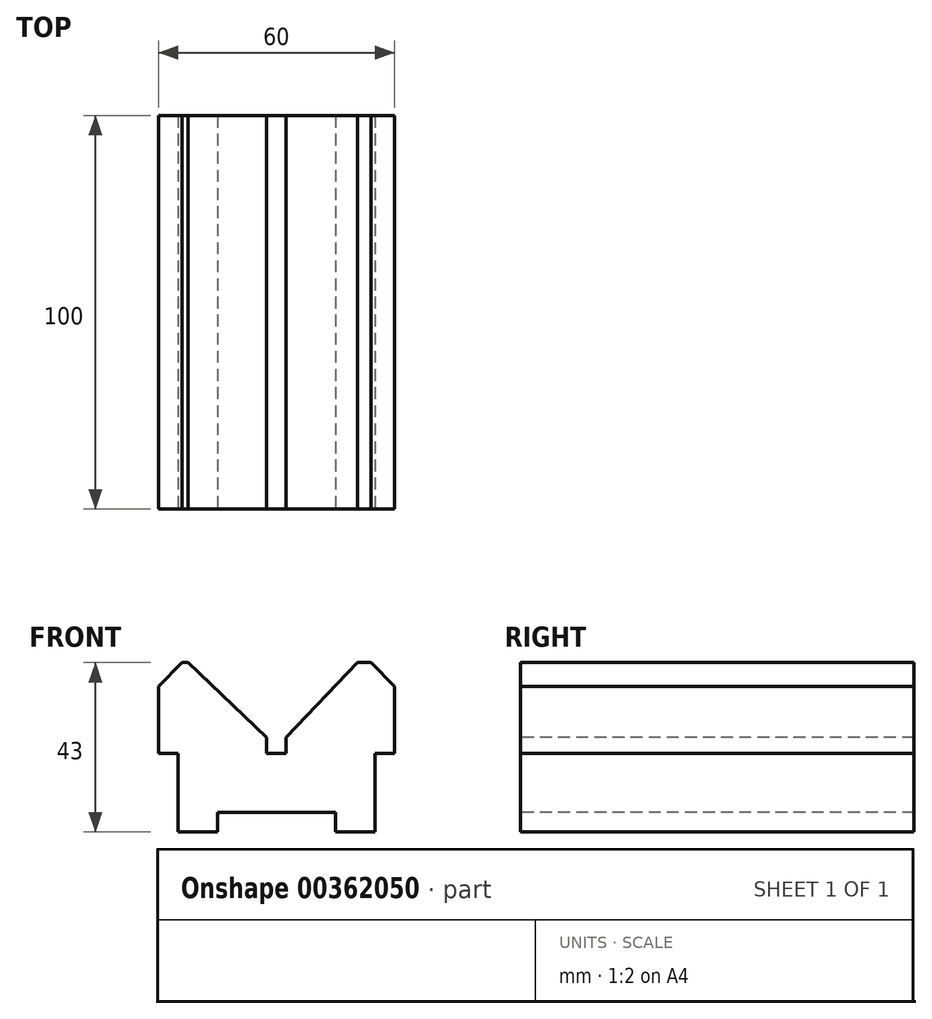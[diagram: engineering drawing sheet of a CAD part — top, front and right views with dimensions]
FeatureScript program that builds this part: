
annotation { "Feature Type Name" : "Feature", "Feature Type Description" : "" }
export const myFeature = defineFeature(function(context is Context, id is Id, definition is map)
    precondition{}
    {
        {
            var Q0;
            Q0=qCreatedBy(makeId("Front.planeOp"),FACE);
            var sketch = newSketch(context, id + "F0", { "sketchPlane" : qUnion([Q0])});
            skLineSegment(sketch, "E0", {"start": v(-24.1, 0) * mm, "end": v(-14.1, 0) * mm});
            skLineSegment(sketch, "E1", {"start": v(-14.1, 0) * mm, "end": v(-14.1, 5) * mm});
            skLineSegment(sketch, "E2", {"start": v(-14.1, 5) * mm, "end": v(15.9, 5) * mm});
            skLineSegment(sketch, "E3", {"start": v(15.9, 5) * mm, "end": v(15.9, 0) * mm});
            skLineSegment(sketch, "E4", {"start": v(15.9, 0) * mm, "end": v(25.9, 0) * mm});
            skLineSegment(sketch, "E5", {"start": v(25.9, 0) * mm, "end": v(25.9, 20) * mm});
            skLineSegment(sketch, "E6", {"start": v(25.9, 20) * mm, "end": v(30.9, 20) * mm});
            skLineSegment(sketch, "E7", {"start": v(30.9, 20) * mm, "end": v(30.9, 37) * mm});
            skLineSegment(sketch, "E8", {"start": v(21.52, 43) * mm, "end": v(3.4, 24.02) * mm});
            skLineSegment(sketch, "E9", {"start": v(3.4, 24.02) * mm, "end": v(3.4, 20) * mm});
            skLineSegment(sketch, "E10", {"start": v(3.4, 20) * mm, "end": v(-1.6, 20) * mm});
            skLineSegment(sketch, "E11", {"start": v(-1.6, 20) * mm, "end": v(-1.6, 24.02) * mm});
            skLineSegment(sketch, "E12", {"start": v(-29.1, 37) * mm, "end": v(-29.1, 20) * mm});
            skLineSegment(sketch, "E13", {"start": v(-29.1, 20) * mm, "end": v(-24.1, 20) * mm});
            skLineSegment(sketch, "E14", {"start": v(-24.1, 20) * mm, "end": v(-24.1, 0) * mm});
            skLineSegment(sketch, "E15", {"start": v(21.52, 43) * mm, "end": v(24.9, 43) * mm});
            skLineSegment(sketch, "E16", {"start": v(24.9, 43) * mm, "end": v(30.9, 37) * mm});
            skLineSegment(sketch, "E17", {"start": v(-29.1, 37) * mm, "end": v(-23.1, 43) * mm});
            skLineSegment(sketch, "E18", {"start": v(-23.1, 43) * mm, "end": v(-21.48, 43) * mm});
            skLineSegment(sketch, "E19", {"start": v(-21.48, 43) * mm, "end": v(-1.6, 24.02) * mm});
            skSolve(sketch);
        }
        {
            var Q0;
            Q0=makeQuery(id+"F0.imprint","IMPRINT",FACE,{"disambiguationData":[TD([[makeQuery(id+"F0.imprint","IMPRINT",EDGE,{"derivedFrom":sQuery(id+"F0.wireOp",EDGE,"E0")}),1.0]])]});
            extrude(context, id + "F1", {"entities" : qUnion([Q0]), "oppositeDirection" : true, "depth" : 100 * mm});
        }
    });
